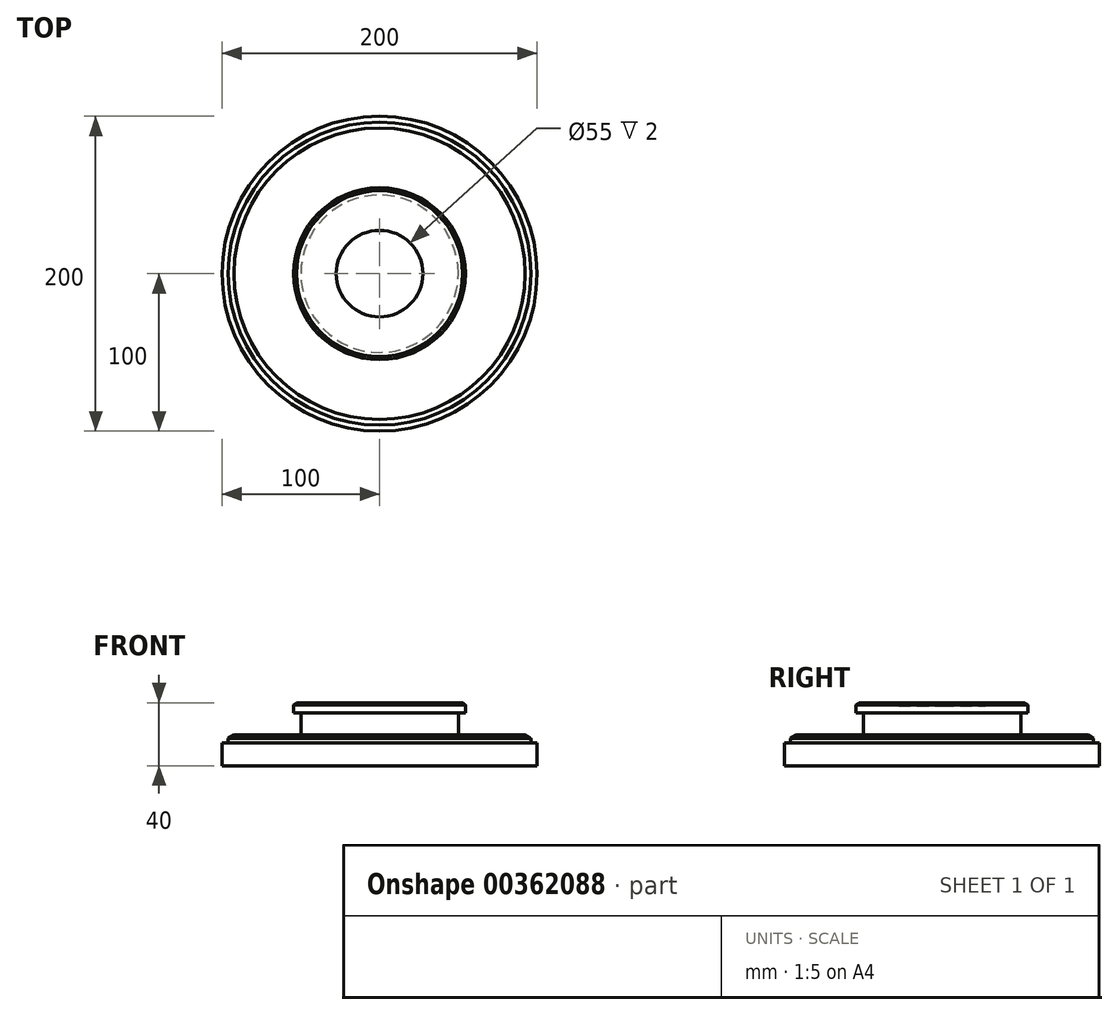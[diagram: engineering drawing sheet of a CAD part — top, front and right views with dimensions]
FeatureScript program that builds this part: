
annotation { "Feature Type Name" : "Feature", "Feature Type Description" : "" }
export const myFeature = defineFeature(function(context is Context, id is Id, definition is map)
    precondition{}
    {
        {
            var Q0;
            Q0=qCreatedBy(makeId("Front.planeOp"),FACE);
            var sketch = newSketch(context, id + "F0", { "sketchPlane" : qUnion([Q0])});
            skLineSegment(sketch, "E0", {"start": v(0, 0) * mm, "end": v(100, 0) * mm});
            skLineSegment(sketch, "E1", {"start": v(100, 0) * mm, "end": v(100, 14.3) * mm});
            skLineSegment(sketch, "E2", {"start": v(100, 14.3) * mm, "end": v(0, 14.3) * mm});
            skLineSegment(sketch, "E3", {"start": v(96.2, 14.3) * mm, "end": v(96.2, 17.26) * mm});
            skLineSegment(sketch, "E4", {"start": v(96.2, 17.26) * mm, "end": v(0, 17.26) * mm});
            skLineSegment(sketch, "E5", {"start": v(96.2, 17.26) * mm, "end": v(92.51, 19.6) * mm});
            skLineSegment(sketch, "E6", {"start": v(92.51, 19.6) * mm, "end": v(0, 19.6) * mm});
            skLineSegment(sketch, "E7", {"start": v(50, 19.6) * mm, "end": v(50, 33.54) * mm});
            skPoint(sketch, "E7.startSnap0", {"position": v(50, 14.3) * mm});
            skLineSegment(sketch, "E8", {"start": v(50, 33.54) * mm, "end": v(0, 33.54) * mm});
            skLineSegment(sketch, "E9", {"start": v(0, 38.54) * mm, "end": v(54.58, 38.54) * mm});
            skLineSegment(sketch, "E10", {"start": v(54.58, 38.54) * mm, "end": v(54.58, 33.54) * mm});
            skLineSegment(sketch, "E11", {"start": v(54.58, 33.54) * mm, "end": v(50, 33.54) * mm});
            skLineSegment(sketch, "E12", {"start": v(54.58, 38.54) * mm, "end": v(52.7, 40) * mm});
            skLineSegment(sketch, "E13", {"start": v(52.7, 40) * mm, "end": v(0, 40) * mm});
            skLineSegment(sketch, "E14", {"start": v(0, 40) * mm, "end": v(0, 0) * mm});
            skPoint(sketch, "E15.orphan", {"position": v(0, 46.6) * mm});
            skSolve(sketch);
        }
        {
            var Q0;
            {var subQ1=sQuery(id+"F0.wireOp",EDGE,"E8");Q0=makeQuery(id+"F0.imprint","IMPRINT",FACE,{"disambiguationData":[TD([[makeQuery(id+"F0.imprint","IMPRINT",EDGE,{"derivedFrom":subQ1}),-1.0]])]});}
            var Q1;
            {var subQ0=sQuery(id+"F0.wireOp",EDGE,"E9");Q1=makeQuery(id+"F0.imprint","IMPRINT",FACE,{"disambiguationData":[TD([[makeQuery(id+"F0.imprint","IMPRINT",EDGE,{"derivedFrom":subQ0}),1.0]])]});}
            var Q2;
            {var subQ3=sQuery(id+"F0.wireOp",EDGE,"E7");Q2=makeQuery(id+"F0.imprint","IMPRINT",FACE,{"disambiguationData":[TD([[makeQuery(id+"F0.imprint","IMPRINT",EDGE,{"derivedFrom":subQ3}),1.0]])]});}
            var Q3;
            {var subQ3=sQuery(id+"F0.wireOp",EDGE,"E3");Q3=makeQuery(id+"F0.imprint","IMPRINT",FACE,{"disambiguationData":[TD([[makeQuery(id+"F0.imprint","IMPRINT",EDGE,{"derivedFrom":subQ3}),1.0]])]});}
            var Q4;
            {var subQ4=sQuery(id+"F0.wireOp",EDGE,"E4");Q4=makeQuery(id+"F0.imprint","IMPRINT",FACE,{"disambiguationData":[TD([[makeQuery(id+"F0.imprint","IMPRINT",EDGE,{"derivedFrom":subQ4}),-1.0]])]});}
            var Q5;
            {var subQ5=sQuery(id+"F0.wireOp",EDGE,"E0");Q5=makeQuery(id+"F0.imprint","IMPRINT",FACE,{"disambiguationData":[TD([[makeQuery(id+"F0.imprint","IMPRINT",EDGE,{"derivedFrom":subQ5}),1.0]])]});}
            var Q6;
            Q6=sQuery(id+"F0.wireOp",EDGE,"E14");
            revolve(context, id + "F1", {"entities" : qUnion([Q0, Q1, Q2, Q3, Q4, Q5]), "axis" : qUnion([Q6]), "revolveType" : RevolveType.FULL});
        }
        {
            var Q0;
            Q0=makeQuery(id+"F1.opRevolve","SWEPT_FACE",FACE,{"disambiguationData":[OSD([sQuery(id+"F0.wireOp",EDGE,"E13")])]});
            var sketch = newSketch(context, id + "F2", { "sketchPlane" : qUnion([Q0])});
            skCircle(sketch, "E16", {"center": v(0, 0) * mm, "radius": 27.5 * mm});
            skSolve(sketch);
        }
        {
            var Q0;
            Q0=makeQuery(id+"F2.imprint","IMPRINT",FACE,{"disambiguationData":[TD([[makeQuery(id+"F2.imprint","IMPRINT",EDGE,{"derivedFrom":sQuery(id+"F2.wireOp",EDGE,"E16")}),1.0]])]});
            extrude(context, id + "F3", {"entities" : qUnion([Q0]), "operationType" : NewBodyOperationType.REMOVE, "oppositeDirection" : true, "depth" : 2 * mm});
        }
    });
